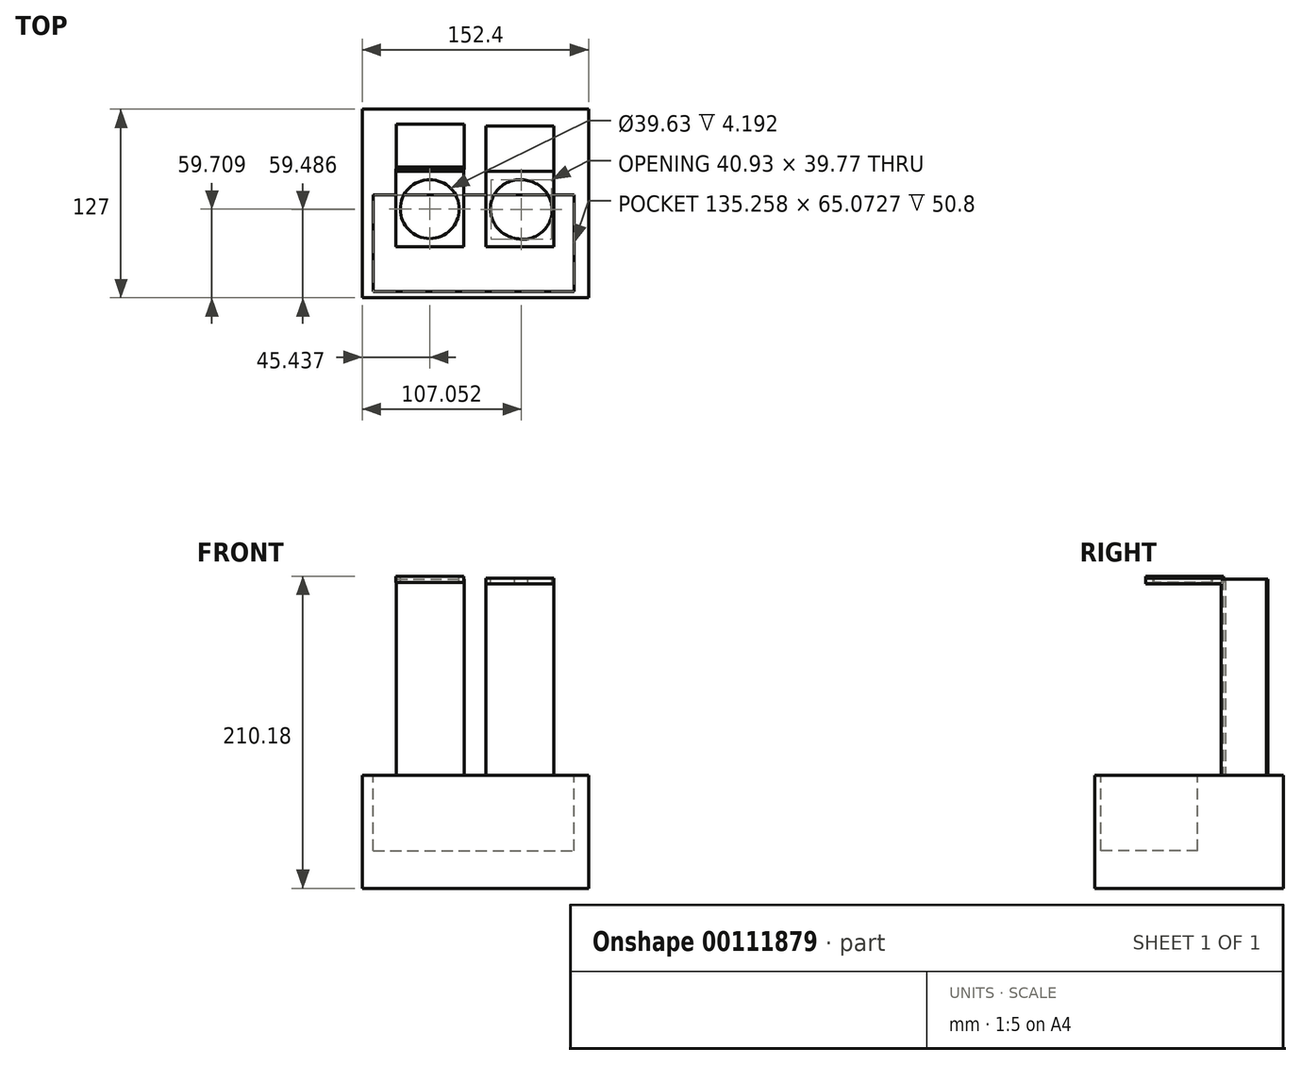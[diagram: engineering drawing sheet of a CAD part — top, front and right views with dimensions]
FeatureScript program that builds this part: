
annotation { "Feature Type Name" : "Feature", "Feature Type Description" : "" }
export const myFeature = defineFeature(function(context is Context, id is Id, definition is map)
    precondition{}
    {
        {
            var Q0;
            Q0=qCreatedBy(makeId("Top.planeOp"),FACE);
            var sketch = newSketch(context, id + "F0", { "sketchPlane" : qUnion([Q0])});
            skLineSegment(sketch, "E0.bottom", {"start": v(-56.17, 48.99) * mm, "end": v(96.23, 48.99) * mm});
            skLineSegment(sketch, "E0.top", {"start": v(-56.17, -78.01) * mm, "end": v(96.23, -78.01) * mm});
            skLineSegment(sketch, "E0.left", {"start": v(-56.17, 48.99) * mm, "end": v(-56.17, -78.01) * mm});
            skLineSegment(sketch, "E0.right", {"start": v(96.23, 48.99) * mm, "end": v(96.23, -78.01) * mm});
            skSolve(sketch);
        }
        {
            var Q0;
            Q0=makeQuery(id+"F0.imprint","IMPRINT",FACE,{"disambiguationData":[TD([[makeQuery(id+"F0.imprint","IMPRINT",EDGE,{"derivedFrom":sQuery(id+"F0.wireOp",EDGE,"E0.bottom")}),-1.0]])]});
            extrude(context, id + "F1", {"entities" : qUnion([Q0]), "depth" : 76.2 * mm});
        }
        {
            var Q0;
            Q0=makeQuery(id+"F1.opExtrude","CAP_FACE",FACE,{"disambiguationData":[OSD([sQuery(id+"F0.wireOp",EDGE,"E0.bottom"),sQuery(id+"F0.wireOp",EDGE,"E0.top"),sQuery(id+"F0.wireOp",EDGE,"E0.left"),sQuery(id+"F0.wireOp",EDGE,"E0.right")])],"isStart":false});
            var sketch = newSketch(context, id + "F2", { "sketchPlane" : qUnion([Q0])});
            skLineSegment(sketch, "E1.bottom", {"start": v(-48.79, -8.6) * mm, "end": v(86.47, -8.6) * mm});
            skLineSegment(sketch, "E1.top", {"start": v(-48.79, -73.67) * mm, "end": v(86.47, -73.67) * mm});
            skLineSegment(sketch, "E1.left", {"start": v(-48.79, -8.6) * mm, "end": v(-48.79, -73.67) * mm});
            skLineSegment(sketch, "E1.right", {"start": v(86.47, -8.6) * mm, "end": v(86.47, -73.67) * mm});
            skSolve(sketch);
        }
        {
            var Q0;
            Q0=makeQuery(id+"F2.imprint","IMPRINT",FACE,{"disambiguationData":[TD([[makeQuery(id+"F2.imprint","IMPRINT",EDGE,{"derivedFrom":sQuery(id+"F2.wireOp",EDGE,"E1.bottom")}),-1.0]])]});
            extrude(context, id + "F3", {"entities" : qUnion([Q0]), "operationType" : NewBodyOperationType.REMOVE, "oppositeDirection" : true, "depth" : 50.8 * mm});
        }
        {
            var Q0;
            Q0=makeQuery(id+"F1.opExtrude","CAP_FACE",FACE,{"disambiguationData":[OSD([sQuery(id+"F0.wireOp",EDGE,"E0.bottom"),sQuery(id+"F0.wireOp",EDGE,"E0.top"),sQuery(id+"F0.wireOp",EDGE,"E0.left"),sQuery(id+"F0.wireOp",EDGE,"E0.right")])],"isStart":false});
            var sketch = newSketch(context, id + "F4", { "sketchPlane" : qUnion([Q0])});
            skLineSegment(sketch, "E2.bottom", {"start": v(-33.21, 38.8) * mm, "end": v(12.5, 38.8) * mm});
            skLineSegment(sketch, "E2.top", {"start": v(-33.21, 8.32) * mm, "end": v(12.5, 8.32) * mm});
            skLineSegment(sketch, "E2.left", {"start": v(-33.21, 38.8) * mm, "end": v(-33.21, 8.32) * mm});
            skLineSegment(sketch, "E2.right", {"start": v(12.5, 38.8) * mm, "end": v(12.5, 8.32) * mm});
            skLineSegment(sketch, "E3.bottom", {"start": v(72.8, 37.58) * mm, "end": v(27.08, 37.58) * mm});
            skLineSegment(sketch, "E3.top", {"start": v(72.8, 7.1) * mm, "end": v(27.08, 7.1) * mm});
            skLineSegment(sketch, "E3.left", {"start": v(72.8, 37.58) * mm, "end": v(72.8, 7.1) * mm});
            skLineSegment(sketch, "E3.right", {"start": v(27.08, 37.58) * mm, "end": v(27.08, 7.1) * mm});
            skSolve(sketch);
        }
        {
            var Q0;
            Q0=makeQuery(id+"F4.imprint","IMPRINT",FACE,{"disambiguationData":[TD([[makeQuery(id+"F4.imprint","IMPRINT",EDGE,{"derivedFrom":sQuery(id+"F4.wireOp",EDGE,"E3.bottom")}),1.0]])]});
            var Q1;
            Q1=makeQuery(id+"F4.imprint","IMPRINT",FACE,{"disambiguationData":[TD([[makeQuery(id+"F4.imprint","IMPRINT",EDGE,{"derivedFrom":sQuery(id+"F4.wireOp",EDGE,"E2.bottom")}),-1.0]])]});
            extrude(context, id + "F5", {"entities" : qUnion([Q0, Q1]), "operationType" : NewBodyOperationType.ADD, "depth" : 132.08 * mm});
        }
        {
            var Q0;
            Q0=makeQuery(id+"F5.opExtrude","SWEPT_FACE",FACE,{"disambiguationData":[OSD([sQuery(id+"F4.wireOp",EDGE,"E3.top")])]});
            var sketch = newSketch(context, id + "F6", { "sketchPlane" : qUnion([Q0])});
            skLineSegment(sketch, "E4.bottom", {"start": v(-33.6, 210.18) * mm, "end": v(12.13, 210.18) * mm});
            skLineSegment(sketch, "E4.top", {"start": v(-33.6, 205.99) * mm, "end": v(12.13, 205.99) * mm});
            skLineSegment(sketch, "E4.left", {"start": v(-33.6, 210.18) * mm, "end": v(-33.6, 205.99) * mm});
            skLineSegment(sketch, "E4.right", {"start": v(12.13, 210.18) * mm, "end": v(12.13, 205.99) * mm});
            skLineSegment(sketch, "E5.bottom", {"start": v(27.08, 209) * mm, "end": v(72.8, 209) * mm});
            skLineSegment(sketch, "E5.top", {"start": v(27.08, 205.2) * mm, "end": v(72.8, 205.2) * mm});
            skLineSegment(sketch, "E5.left", {"start": v(27.08, 209) * mm, "end": v(27.08, 205.2) * mm});
            skLineSegment(sketch, "E5.right", {"start": v(72.8, 209) * mm, "end": v(72.8, 205.2) * mm});
            skSolve(sketch);
        }
        {
            var Q0;
            Q0=qSketchRegion(id+"F6",true);
            extrude(context, id + "F7", {"entities" : qUnion([Q0]), "operationType" : NewBodyOperationType.ADD, "depth" : 50.8 * mm});
        }
        {
            var Q0;
            Q0=makeQuery(id+"F7.opExtrude","SWEPT_FACE",FACE,{"disambiguationData":[OSD([sQuery(id+"F6.wireOp",EDGE,"E4.bottom")])]});
            var sketch = newSketch(context, id + "F8", { "sketchPlane" : qUnion([Q0])});
            skCircle(sketch, "E6", {"center": v(-10.73, -18.3) * mm, "radius": 19.81 * mm});
            skCircle(sketch, "E7", {"center": v(51.83, -18.75) * mm, "radius": 19.81 * mm});
            skSolve(sketch);
        }
        {
            var Q0;
            Q0=makeQuery(id+"F8.imprint","IMPRINT",FACE,{"disambiguationData":[TD([[makeQuery(id+"F8.imprint","IMPRINT",EDGE,{"derivedFrom":sQuery(id+"F8.wireOp",EDGE,"E6")}),1.0]])]});
            var Q1;
            Q1=makeQuery(id+"F8.imprint","IMPRINT",FACE,{"disambiguationData":[TD([[makeQuery(id+"F8.imprint","IMPRINT",EDGE,{"derivedFrom":sQuery(id+"F8.wireOp",EDGE,"E7")}),1.0]])]});
            var Q2;
            Q2=sQuery(id+"F8.wireOp",EDGE,"E7");
            var Q3;
            Q3=sQuery(id+"F8.wireOp",EDGE,"E6");
            extrude(context, id + "F9", {"entities" : qUnion([Q0, Q1]), "operationType" : NewBodyOperationType.REMOVE, "surfaceEntities" : qUnion([Q2, Q3]), "oppositeDirection" : true, "depth" : 25.4 * mm});
        }
        {
            var Q0;
            Q0=makeQuery(id+"F7.opExtrude","SWEPT_FACE",FACE,{"disambiguationData":[OSD([sQuery(id+"F6.wireOp",EDGE,"E5.bottom")])]});
            var sketch = newSketch(context, id + "F10", { "sketchPlane" : qUnion([Q0])});
            skCircle(sketch, "E8", {"center": v(49.94, -18.3) * mm, "radius": 19.81 * mm});
            skSolve(sketch);
        }
        {
            var Q0;
            Q0=makeQuery(id+"F10.imprint","IMPRINT",FACE,{"disambiguationData":[TD([[makeQuery(id+"F10.imprint","IMPRINT",EDGE,{"derivedFrom":sQuery(id+"F10.wireOp",EDGE,"E8")}),1.0]])]});
            extrude(context, id + "F11", {"entities" : qUnion([Q0]), "operationType" : NewBodyOperationType.REMOVE, "oppositeDirection" : true, "depth" : 25.4 * mm});
        }
        {
            var Q0;
            Q0=makeQuery(id+"F7.opExtrude","CAP_FACE",FACE,{"disambiguationData":[OSD([sQuery(id+"F6.wireOp",EDGE,"E4.bottom"),sQuery(id+"F6.wireOp",EDGE,"E4.top"),sQuery(id+"F6.wireOp",EDGE,"E4.left"),sQuery(id+"F6.wireOp",EDGE,"E4.right")])],"isStart":true});
            var Q1;
            Q1=makeQuery(id+"F5.opExtrude","SWEPT_FACE",FACE,{"disambiguationData":[OSD([sQuery(id+"F4.wireOp",EDGE,"E2.top")])]});
            extrude(context, id + "F12", {"entities" : qUnion([Q0, Q1]), "depth" : 1.78 * mm});
        }
    });
